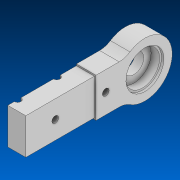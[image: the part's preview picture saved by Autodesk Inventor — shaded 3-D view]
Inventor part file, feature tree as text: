
AUTODESK INVENTOR PART (.ipt)
format: ipt  version: 2022.2 (Build 262287000, 287)  size: 159,232 bytes
history: native  units: in
note: dims shown in document units (in); Inventor stores cm internally (conversion verified against a paired STEP export)
features: extrude x4, sketch x3, hole x2
ambient origin geometry x8: Origin, YZ Plane, XZ Plane, XY Plane, X Axis, Y Axis, Z Axis, Center Point
bodies: Solid1 (feature_tree)
feature tree (9):
  sketch  "Sketch1"  dims[d1=0.969in d2=0.302in]
  extrude  "Extrusion1"  Depth=0.302in
  extrude  "Extrusion2"  Depth=1.0in
  extrude  "Extrusion3"  Depth=1.75in
  extrude  "Extrusion4"  Depth=0.46in TaperAngle=0.0deg
  hole  "Hole1"  [1 undecoded]
  hole  "Hole2"  [1 undecoded]
  sketch  "Sketch2"  dims[d3=0.875in d5=1.0in]
  sketch  "Sketch3"  dims[d7=0.5in d8=1.75in d9=0.46in d10=0.0in d11=0.5in d12=0.0in d13=0.5in d14=0.22in d15=0.0in d16=0.438in d17=0.0in d19=1.0in d20=0.17in d21=0.75in d22=0.375in d23=0.25in d24=0.5635in d25=1.0in d26=0.0in d27=0.04in d29=1.25in d30=0.17in d31=0.75in d32=0.375in d33=0.25in d34=0.5635in d35=1.0in d36=0.0in d37=1.0in d38=0.5in d39=1.25in d40=1.0in]
note: 2 required parameter values undecoded (feature->parameter linkage not recoverable at this tier; creation-order binding heuristic only, values carry confidence <= 0.55)
